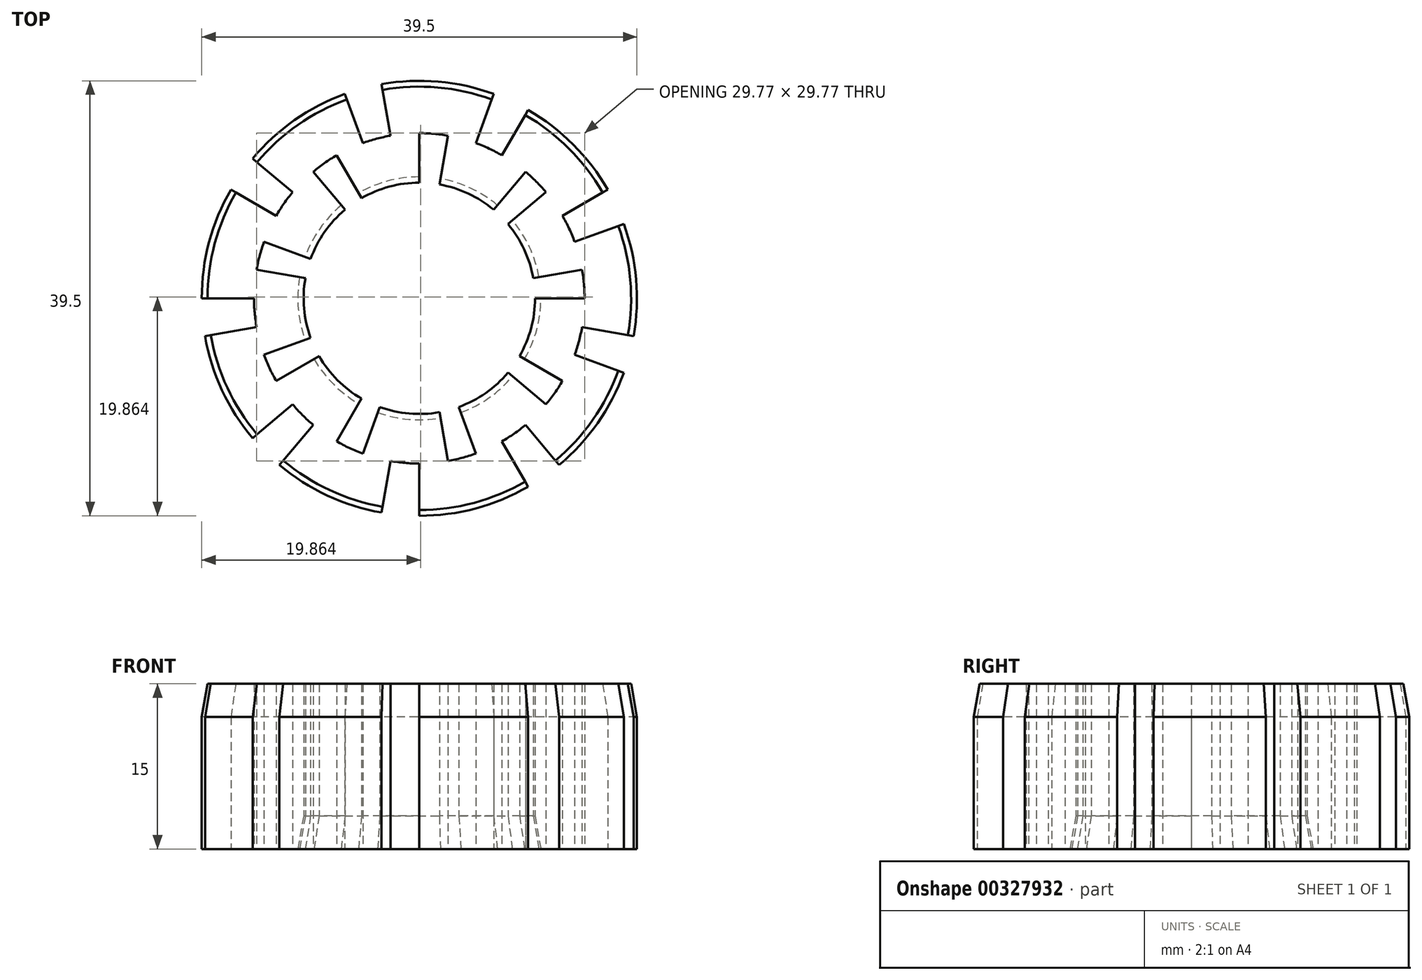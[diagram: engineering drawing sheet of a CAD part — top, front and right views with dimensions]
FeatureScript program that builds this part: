
annotation { "Feature Type Name" : "Feature", "Feature Type Description" : "" }
export const myFeature = defineFeature(function(context is Context, id is Id, definition is map)
    precondition{}
    {
        {
            var Q0;
            Q0=qCreatedBy(makeId("Top.planeOp"),FACE);
            var sketch = newSketch(context, id + "F0", { "sketchPlane" : qUnion([Q0])});
            skArc(sketch, "E0", {"start": v(-6.75, 18.56) * mm, "mid": v(-11.33, 16.18) * mm, "end": v(-15.13, 12.7) * mm});
            skArc(sketch, "E1", {"start": v(9.1, -5.25) * mm, "mid": v(10.14, -2.72) * mm, "end": v(10.5, 0) * mm});
            skLineSegment(sketch, "E2", {"start": v(0, 10.5) * mm, "end": v(0, 15) * mm});
            skArc(sketch, "E3", {"start": v(2.6, -14.77) * mm, "mid": v(3.88, -14.49) * mm, "end": v(5.13, -14.1) * mm});
            skLineSegment(sketch, "E4.1.0", {"start": v(-2.6, 14.77) * mm, "end": v(-3.43, 19.45) * mm});
            skLineSegment(sketch, "E4.2.0", {"start": v(-5.13, 14.1) * mm, "end": v(-6.75, 18.56) * mm});
            skLineSegment(sketch, "E4.3.0", {"start": v(-5.25, 9.1) * mm, "end": v(-7.5, 13) * mm});
            skLineSegment(sketch, "E4.4.0", {"start": v(-6.75, 8.04) * mm, "end": v(-9.64, 11.5) * mm});
            skLineSegment(sketch, "E4.5.0", {"start": v(-11.5, 9.64) * mm, "end": v(-15.13, 12.7) * mm});
            skLineSegment(sketch, "E4.6.0", {"start": v(-13, 7.5) * mm, "end": v(-17.1, 9.88) * mm});
            skLineSegment(sketch, "E4.7.0", {"start": v(-9.87, 3.6) * mm, "end": v(-14.1, 5.13) * mm});
            skLineSegment(sketch, "E4.8.0", {"start": v(-10.34, 1.82) * mm, "end": v(-14.77, 2.6) * mm});
            skLineSegment(sketch, "E4.9.0", {"start": v(-15, 0) * mm, "end": v(-19.75, 0) * mm});
            skLineSegment(sketch, "E4.10.0", {"start": v(-14.77, -2.6) * mm, "end": v(-19.45, -3.43) * mm});
            skLineSegment(sketch, "E4.11.0", {"start": v(-9.87, -3.6) * mm, "end": v(-14.1, -5.13) * mm});
            skLineSegment(sketch, "E4.12.0", {"start": v(-9.1, -5.25) * mm, "end": v(-13, -7.5) * mm});
            skLineSegment(sketch, "E4.13.0", {"start": v(-11.5, -9.64) * mm, "end": v(-15.13, -12.7) * mm});
            skLineSegment(sketch, "E4.14.0", {"start": v(-9.64, -11.5) * mm, "end": v(-12.7, -15.13) * mm});
            skLineSegment(sketch, "E4.15.0", {"start": v(-5.25, -9.1) * mm, "end": v(-7.5, -13) * mm});
            skLineSegment(sketch, "E4.16.0", {"start": v(-3.6, -9.87) * mm, "end": v(-5.13, -14.1) * mm});
            skLineSegment(sketch, "E4.17.0", {"start": v(-2.6, -14.77) * mm, "end": v(-3.43, -19.45) * mm});
            skLineSegment(sketch, "E4.18.0", {"start": v(0, -15) * mm, "end": v(0, -19.75) * mm});
            skLineSegment(sketch, "E4.19.0", {"start": v(1.82, -10.34) * mm, "end": v(2.6, -14.77) * mm});
            skLineSegment(sketch, "E4.20.0", {"start": v(3.6, -9.87) * mm, "end": v(5.13, -14.1) * mm});
            skLineSegment(sketch, "E4.21.0", {"start": v(7.5, -13) * mm, "end": v(9.88, -17.1) * mm});
            skLineSegment(sketch, "E4.22.0", {"start": v(9.64, -11.5) * mm, "end": v(12.7, -15.13) * mm});
            skLineSegment(sketch, "E4.23.0", {"start": v(8.04, -6.75) * mm, "end": v(11.5, -9.64) * mm});
            skLineSegment(sketch, "E4.24.0", {"start": v(9.1, -5.25) * mm, "end": v(13, -7.5) * mm});
            skLineSegment(sketch, "E4.25.0", {"start": v(14.1, -5.13) * mm, "end": v(18.56, -6.75) * mm});
            skLineSegment(sketch, "E4.26.0", {"start": v(14.77, -2.6) * mm, "end": v(19.45, -3.43) * mm});
            skLineSegment(sketch, "E4.27.0", {"start": v(10.5, 0) * mm, "end": v(15, 0) * mm});
            skLineSegment(sketch, "E4.28.0", {"start": v(10.34, 1.82) * mm, "end": v(14.77, 2.6) * mm});
            skLineSegment(sketch, "E4.29.0", {"start": v(14.1, 5.13) * mm, "end": v(18.56, 6.75) * mm});
            skLineSegment(sketch, "E4.30.0", {"start": v(13, 7.5) * mm, "end": v(17.1, 9.87) * mm});
            skLineSegment(sketch, "E4.31.0", {"start": v(8.04, 6.75) * mm, "end": v(11.5, 9.64) * mm});
            skLineSegment(sketch, "E4.32.0", {"start": v(6.75, 8.04) * mm, "end": v(9.64, 11.5) * mm});
            skLineSegment(sketch, "E4.33.0", {"start": v(7.5, 13) * mm, "end": v(9.87, 17.1) * mm});
            skLineSegment(sketch, "E4.34.0", {"start": v(5.13, 14.1) * mm, "end": v(6.75, 18.56) * mm});
            skLineSegment(sketch, "E4.35.0", {"start": v(1.82, 10.34) * mm, "end": v(2.6, 14.77) * mm});
            skArc(sketch, "E5.trimOffspring", {"start": v(6.75, 18.56) * mm, "mid": v(1.72, 19.67) * mm, "end": v(-3.43, 19.45) * mm});
            skArc(sketch, "E6.trimOffspring", {"start": v(17.1, 9.87) * mm, "mid": v(13.97, 13.97) * mm, "end": v(9.88, 17.1) * mm});
            skArc(sketch, "E7.trimOffspring", {"start": v(19.45, -3.43) * mm, "mid": v(19.67, 1.72) * mm, "end": v(18.56, 6.75) * mm});
            skArc(sketch, "E8.trimOffspring", {"start": v(-17.1, 9.88) * mm, "mid": v(-19.08, 5.11) * mm, "end": v(-19.75, 0) * mm});
            skArc(sketch, "E9.trimOffspring", {"start": v(-19.45, -3.43) * mm, "mid": v(-17.9, -8.35) * mm, "end": v(-15.13, -12.7) * mm});
            skArc(sketch, "E10.trimOffspring", {"start": v(-12.7, -15.13) * mm, "mid": v(-8.35, -17.9) * mm, "end": v(-3.43, -19.45) * mm});
            skArc(sketch, "E11.trimOffspring", {"start": v(0, -19.75) * mm, "mid": v(5.11, -19.08) * mm, "end": v(9.88, -17.1) * mm});
            skArc(sketch, "E12.trimOffspring", {"start": v(12.7, -15.13) * mm, "mid": v(16.18, -11.33) * mm, "end": v(18.56, -6.75) * mm});
            skArc(sketch, "E13.trimOffspring", {"start": v(10.34, 1.82) * mm, "mid": v(9.52, 4.44) * mm, "end": v(8.04, 6.75) * mm});
            skArc(sketch, "E14.trimOffspring", {"start": v(6.75, 8.04) * mm, "mid": v(4.44, 9.52) * mm, "end": v(1.82, 10.34) * mm});
            skArc(sketch, "E15.trimOffspring", {"start": v(0, 10.5) * mm, "mid": v(-2.72, 10.14) * mm, "end": v(-5.25, 9.1) * mm});
            skArc(sketch, "E16.trimOffspring", {"start": v(-6.75, 8.04) * mm, "mid": v(-8.6, 6.02) * mm, "end": v(-9.87, 3.6) * mm});
            skArc(sketch, "E17.trimOffspring", {"start": v(-10.34, 1.82) * mm, "mid": v(-10.46, -0.92) * mm, "end": v(-9.87, -3.6) * mm});
            skArc(sketch, "E18.trimOffspring", {"start": v(-9.1, -5.25) * mm, "mid": v(-7.42, -7.42) * mm, "end": v(-5.25, -9.1) * mm});
            skArc(sketch, "E19.trimOffspring", {"start": v(-3.6, -9.87) * mm, "mid": v(-0.92, -10.46) * mm, "end": v(1.82, -10.34) * mm});
            skArc(sketch, "E20.trimOffspring", {"start": v(3.6, -9.87) * mm, "mid": v(6.02, -8.6) * mm, "end": v(8.04, -6.75) * mm});
            skArc(sketch, "E21.trimOffspring", {"start": v(-2.6, -14.77) * mm, "mid": v(-1.3, -14.94) * mm, "end": v(0, -15) * mm});
            skArc(sketch, "E22.trimOffspring", {"start": v(-7.5, -13) * mm, "mid": v(-6.34, -13.6) * mm, "end": v(-5.13, -14.1) * mm});
            skArc(sketch, "E23.trimOffspring", {"start": v(-11.5, -9.64) * mm, "mid": v(-10.6, -10.6) * mm, "end": v(-9.64, -11.5) * mm});
            skArc(sketch, "E24.trimOffspring", {"start": v(-14.1, -5.13) * mm, "mid": v(-13.6, -6.34) * mm, "end": v(-13, -7.5) * mm});
            skArc(sketch, "E25.trimOffspring", {"start": v(-15, 0) * mm, "mid": v(-14.94, -1.3) * mm, "end": v(-14.77, -2.6) * mm});
            skArc(sketch, "E26.trimOffspring", {"start": v(-14.1, 5.13) * mm, "mid": v(-14.49, 3.88) * mm, "end": v(-14.77, 2.6) * mm});
            skArc(sketch, "E27.trimOffspring", {"start": v(-11.5, 9.64) * mm, "mid": v(-12.29, 8.6) * mm, "end": v(-13, 7.5) * mm});
            skArc(sketch, "E28.trimOffspring", {"start": v(-7.5, 13) * mm, "mid": v(-8.6, 12.29) * mm, "end": v(-9.64, 11.5) * mm});
            skArc(sketch, "E29.trimOffspring", {"start": v(-2.6, 14.77) * mm, "mid": v(-3.88, 14.49) * mm, "end": v(-5.13, 14.1) * mm});
            skArc(sketch, "E30.trimOffspring", {"start": v(2.6, 14.77) * mm, "mid": v(1.3, 14.94) * mm, "end": v(0, 15) * mm});
            skArc(sketch, "E31.trimOffspring", {"start": v(7.5, 13) * mm, "mid": v(6.34, 13.6) * mm, "end": v(5.13, 14.1) * mm});
            skArc(sketch, "E32.trimOffspring", {"start": v(11.5, 9.64) * mm, "mid": v(10.6, 10.6) * mm, "end": v(9.64, 11.5) * mm});
            skArc(sketch, "E33.trimOffspring", {"start": v(14.1, 5.13) * mm, "mid": v(13.6, 6.34) * mm, "end": v(13, 7.5) * mm});
            skArc(sketch, "E34.trimOffspring", {"start": v(15, 0) * mm, "mid": v(14.94, 1.3) * mm, "end": v(14.77, 2.6) * mm});
            skArc(sketch, "E35.trimOffspring", {"start": v(14.1, -5.13) * mm, "mid": v(14.49, -3.88) * mm, "end": v(14.77, -2.6) * mm});
            skArc(sketch, "E36.trimOffspring", {"start": v(11.5, -9.64) * mm, "mid": v(12.29, -8.6) * mm, "end": v(13, -7.5) * mm});
            skArc(sketch, "E37.trimOffspring", {"start": v(7.5, -13) * mm, "mid": v(8.6, -12.29) * mm, "end": v(9.64, -11.5) * mm});
            skPoint(sketch, "E38.orphan", {"position": v(3.43, -19.45) * mm});
            skPoint(sketch, "E39.orphan", {"position": v(6.75, -18.56) * mm});
            skPoint(sketch, "E40.orphan", {"position": v(15.13, -12.7) * mm});
            skPoint(sketch, "E41.orphan", {"position": v(17.1, -9.88) * mm});
            skPoint(sketch, "E42.orphan", {"position": v(15.13, 12.7) * mm});
            skPoint(sketch, "E43.orphan", {"position": v(12.7, 15.13) * mm});
            skPoint(sketch, "E44.orphan", {"position": v(-17.1, -9.87) * mm});
            skPoint(sketch, "E45.orphan", {"position": v(-18.56, -6.75) * mm});
            skPoint(sketch, "E46.orphan", {"position": v(-9.88, -17.1) * mm});
            skPoint(sketch, "E47.orphan", {"position": v(-6.75, -18.56) * mm});
            skPoint(sketch, "E48.orphan", {"position": v(-19.45, 3.43) * mm});
            skPoint(sketch, "E49.orphan", {"position": v(-18.56, 6.75) * mm});
            skPoint(sketch, "E50.orphan", {"position": v(-12.7, 15.13) * mm});
            skPoint(sketch, "E51.orphan", {"position": v(-9.87, 17.1) * mm});
            skPoint(sketch, "E52.orphan", {"position": v(0, 19.75) * mm});
            skPoint(sketch, "E53.orphan", {"position": v(3.43, 19.45) * mm});
            skPoint(sketch, "E54.orphan", {"position": v(19.75, 0) * mm});
            skPoint(sketch, "E55.orphan", {"position": v(19.45, 3.43) * mm});
            skSolve(sketch);
        }
        {
            var Q0;
            Q0 = qSketchRegion(id + "F0", true);
            extrude(context, id + "F1", {"entities" : qUnion([Q0]), "depth" : 15 * mm});
        }
        {
            var Q0;
            Q0=makeQuery(id+"F1.opExtrude","CAP_EDGE",EDGE,{"disambiguationData":[OSD([sQuery(id+"F0.wireOp",EDGE,"E11.trimOffspring")])],"isStart":false});
            var Q1;
            Q1=makeQuery(id+"F1.opExtrude","CAP_EDGE",EDGE,{"disambiguationData":[OSD([sQuery(id+"F0.wireOp",EDGE,"E12.trimOffspring")])],"isStart":false});
            var Q2;
            Q2=makeQuery(id+"F1.opExtrude","CAP_EDGE",EDGE,{"disambiguationData":[OSD([sQuery(id+"F0.wireOp",EDGE,"E7.trimOffspring")])],"isStart":false});
            var Q3;
            Q3=makeQuery(id+"F1.opExtrude","CAP_EDGE",EDGE,{"disambiguationData":[OSD([sQuery(id+"F0.wireOp",EDGE,"E6.trimOffspring")])],"isStart":false});
            var Q4;
            Q4=makeQuery(id+"F1.opExtrude","CAP_EDGE",EDGE,{"disambiguationData":[OSD([sQuery(id+"F0.wireOp",EDGE,"E5.trimOffspring")])],"isStart":false});
            var Q5;
            Q5=makeQuery(id+"F1.opExtrude","CAP_EDGE",EDGE,{"disambiguationData":[OSD([sQuery(id+"F0.wireOp",EDGE,"E0")])],"isStart":false});
            var Q6;
            Q6=makeQuery(id+"F1.opExtrude","CAP_EDGE",EDGE,{"disambiguationData":[OSD([sQuery(id+"F0.wireOp",EDGE,"E8.trimOffspring")])],"isStart":false});
            var Q7;
            Q7=makeQuery(id+"F1.opExtrude","CAP_EDGE",EDGE,{"disambiguationData":[OSD([sQuery(id+"F0.wireOp",EDGE,"E9.trimOffspring")])],"isStart":false});
            var Q8;
            Q8=makeQuery(id+"F1.opExtrude","CAP_EDGE",EDGE,{"disambiguationData":[OSD([sQuery(id+"F0.wireOp",EDGE,"E10.trimOffspring")])],"isStart":false});
            chamfer(context, id + "F2", {"entities" : qUnion([Q0, Q1, Q2, Q3, Q4, Q5, Q6, Q7, Q8]), "chamferType" : ChamferType.OFFSET_ANGLE, "width" : 3 * mm, "oppositeDirection" : true, "angle" : 10 * degree, "tangentPropagation" : true});
        }
        {
            var Q0;
            Q0=makeQuery(id+"F1.opExtrude","CAP_EDGE",EDGE,{"disambiguationData":[OSD([sQuery(id+"F0.wireOp",EDGE,"E19.trimOffspring")])],"isStart":true});
            var Q1;
            Q1=makeQuery(id+"F1.opExtrude","CAP_EDGE",EDGE,{"disambiguationData":[OSD([sQuery(id+"F0.wireOp",EDGE,"E18.trimOffspring")])],"isStart":true});
            var Q2;
            Q2=makeQuery(id+"F1.opExtrude","CAP_EDGE",EDGE,{"disambiguationData":[OSD([sQuery(id+"F0.wireOp",EDGE,"E17.trimOffspring")])],"isStart":true});
            var Q3;
            Q3=makeQuery(id+"F1.opExtrude","CAP_EDGE",EDGE,{"disambiguationData":[OSD([sQuery(id+"F0.wireOp",EDGE,"E16.trimOffspring")])],"isStart":true});
            var Q4;
            Q4=makeQuery(id+"F1.opExtrude","CAP_EDGE",EDGE,{"disambiguationData":[OSD([sQuery(id+"F0.wireOp",EDGE,"E15.trimOffspring")])],"isStart":true});
            var Q5;
            Q5=makeQuery(id+"F1.opExtrude","CAP_EDGE",EDGE,{"disambiguationData":[OSD([sQuery(id+"F0.wireOp",EDGE,"E14.trimOffspring")])],"isStart":true});
            var Q6;
            Q6=makeQuery(id+"F1.opExtrude","CAP_EDGE",EDGE,{"disambiguationData":[OSD([sQuery(id+"F0.wireOp",EDGE,"E13.trimOffspring")])],"isStart":true});
            var Q7;
            Q7=makeQuery(id+"F1.opExtrude","CAP_EDGE",EDGE,{"disambiguationData":[OSD([sQuery(id+"F0.wireOp",EDGE,"E1")])],"isStart":true});
            var Q8;
            Q8=makeQuery(id+"F1.opExtrude","CAP_EDGE",EDGE,{"disambiguationData":[OSD([sQuery(id+"F0.wireOp",EDGE,"E20.trimOffspring")])],"isStart":true});
            chamfer(context, id + "F3", {"entities" : qUnion([Q0, Q1, Q2, Q3, Q4, Q5, Q6, Q7, Q8]), "chamferType" : ChamferType.OFFSET_ANGLE, "width" : 3 * mm, "oppositeDirection" : true, "angle" : 10 * degree, "tangentPropagation" : true});
        }
    });
